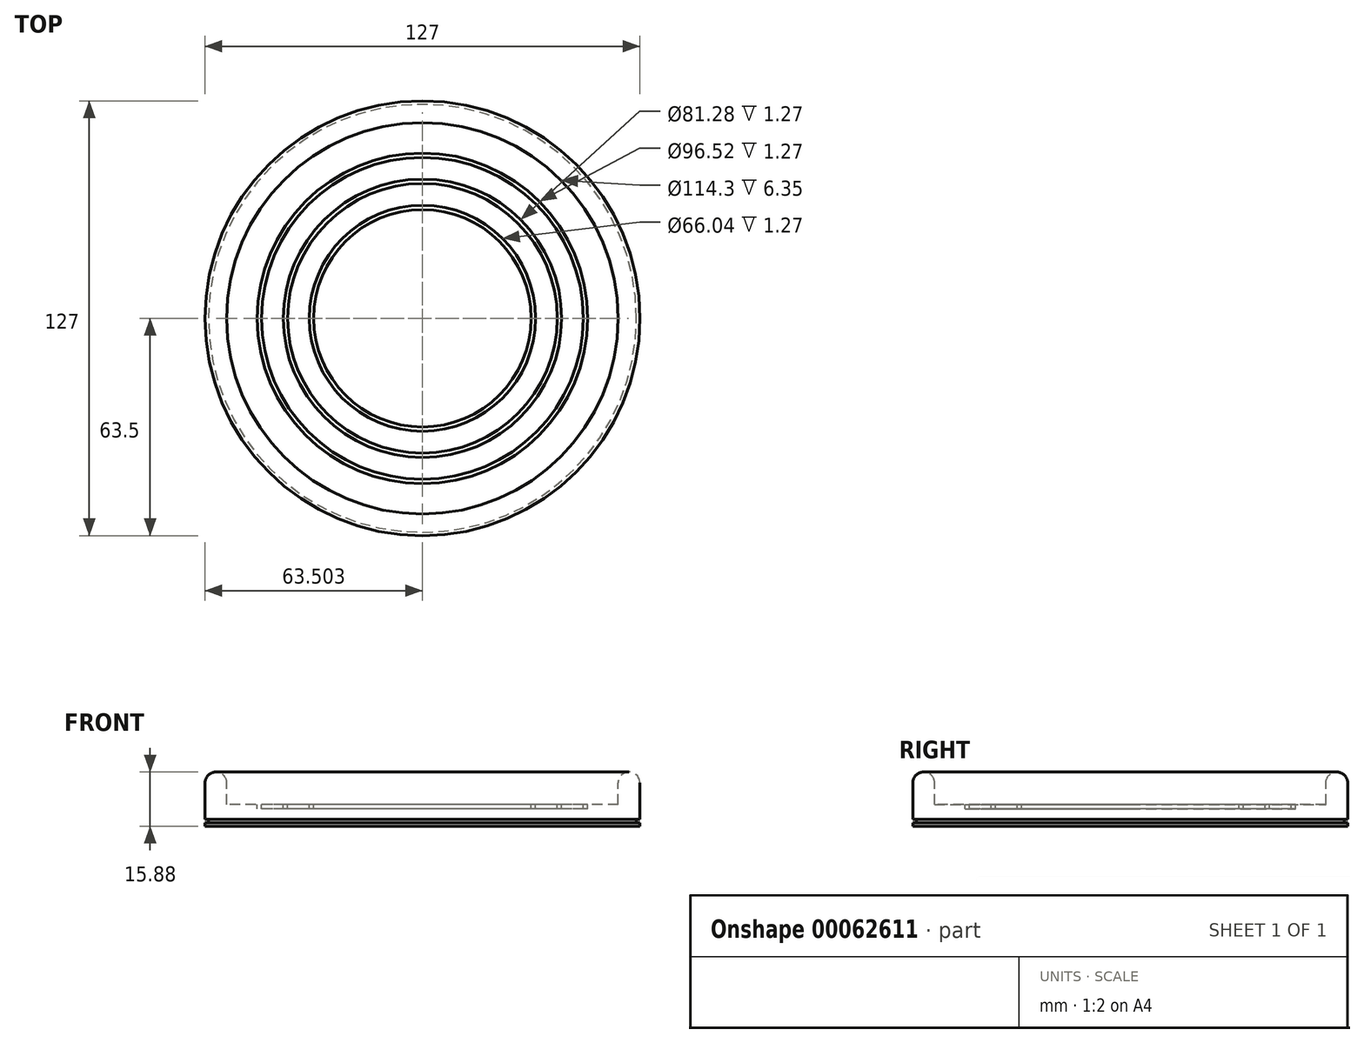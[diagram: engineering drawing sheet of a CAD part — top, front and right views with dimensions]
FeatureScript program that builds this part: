
annotation { "Feature Type Name" : "Feature", "Feature Type Description" : "" }
export const myFeature = defineFeature(function(context is Context, id is Id, definition is map)
    precondition{}
    {
        {
            var Q0;
            Q0=qCreatedBy(makeId("Front.planeOp"),FACE);
            var sketch = newSketch(context, id + "F0", { "sketchPlane" : qUnion([Q0])});
            skLineSegment(sketch, "E0", {"start": v(36.74, 8.75) * mm, "end": v(36.74, 2.4) * mm});
            skLineSegment(sketch, "E1", {"start": v(36.74, 2.4) * mm, "end": v(-26.76, 2.4) * mm});
            skLineSegment(sketch, "E2", {"start": v(-26.76, 2.4) * mm, "end": v(-26.76, 3.42) * mm});
            skLineSegment(sketch, "E3", {"start": v(-20.4, 8.75) * mm, "end": v(-20.4, 15.1) * mm});
            skArc(sketch, "E4", {"start": v(-20.4, 15.1) * mm, "mid": v(-23.58, 18.28) * mm, "end": v(-26.76, 15.1) * mm});
            skLineSegment(sketch, "E5", {"start": v(-20.4, 8.75) * mm, "end": v(-11.52, 8.75) * mm});
            skLineSegment(sketch, "E6.top", {"start": v(-11.52, 7.48) * mm, "end": v(-10.25, 7.48) * mm});
            skLineSegment(sketch, "E6.left", {"start": v(-11.52, 8.75) * mm, "end": v(-11.52, 7.48) * mm});
            skLineSegment(sketch, "E6.right", {"start": v(-10.25, 8.75) * mm, "end": v(-10.25, 7.48) * mm});
            skLineSegment(sketch, "E7.top", {"start": v(-3.9, 7.48) * mm, "end": v(-2.63, 7.48) * mm});
            skLineSegment(sketch, "E7.left", {"start": v(-3.9, 8.75) * mm, "end": v(-3.9, 7.48) * mm});
            skLineSegment(sketch, "E8.top", {"start": v(3.72, 7.48) * mm, "end": v(5, 7.48) * mm});
            skLineSegment(sketch, "E9", {"start": v(-10.25, 8.75) * mm, "end": v(-3.9, 8.75) * mm});
            skLineSegment(sketch, "E10", {"start": v(5, 8.75) * mm, "end": v(5, 7.48) * mm});
            skLineSegment(sketch, "E11", {"start": v(5, 8.75) * mm, "end": v(36.74, 8.75) * mm});
            skLineSegment(sketch, "E12", {"start": v(-2.63, 7.48) * mm, "end": v(-2.63, 8.75) * mm});
            skLineSegment(sketch, "E13", {"start": v(-2.63, 8.75) * mm, "end": v(3.72, 8.75) * mm});
            skLineSegment(sketch, "E14", {"start": v(3.72, 8.75) * mm, "end": v(3.72, 7.48) * mm});
            skLineSegment(sketch, "E15.bottom", {"start": v(-26.76, 4.43) * mm, "end": v(-25.74, 4.43) * mm});
            skLineSegment(sketch, "E15.top", {"start": v(-26.76, 3.42) * mm, "end": v(-25.74, 3.42) * mm});
            skLineSegment(sketch, "E15.right", {"start": v(-25.74, 4.43) * mm, "end": v(-25.74, 3.42) * mm});
            skLineSegment(sketch, "E16", {"start": v(-26.76, 4.43) * mm, "end": v(-26.76, 15.1) * mm});
            skSolve(sketch);
        }
        {
            var Q0;
            Q0=makeQuery(id+"F0.imprint","IMPRINT",FACE,{"disambiguationData":[TD([[makeQuery(id+"F0.imprint","IMPRINT",EDGE,{"derivedFrom":sQuery(id+"F0.wireOp",EDGE,"E0")}),-1.0]])]});
            var Q1;
            Q1=sQuery(id+"F0.wireOp",EDGE,"E0");
            revolve(context, id + "F1", {"entities" : qUnion([Q0]), "axis" : qUnion([Q1]), "revolveType" : RevolveType.FULL});
        }
    });
